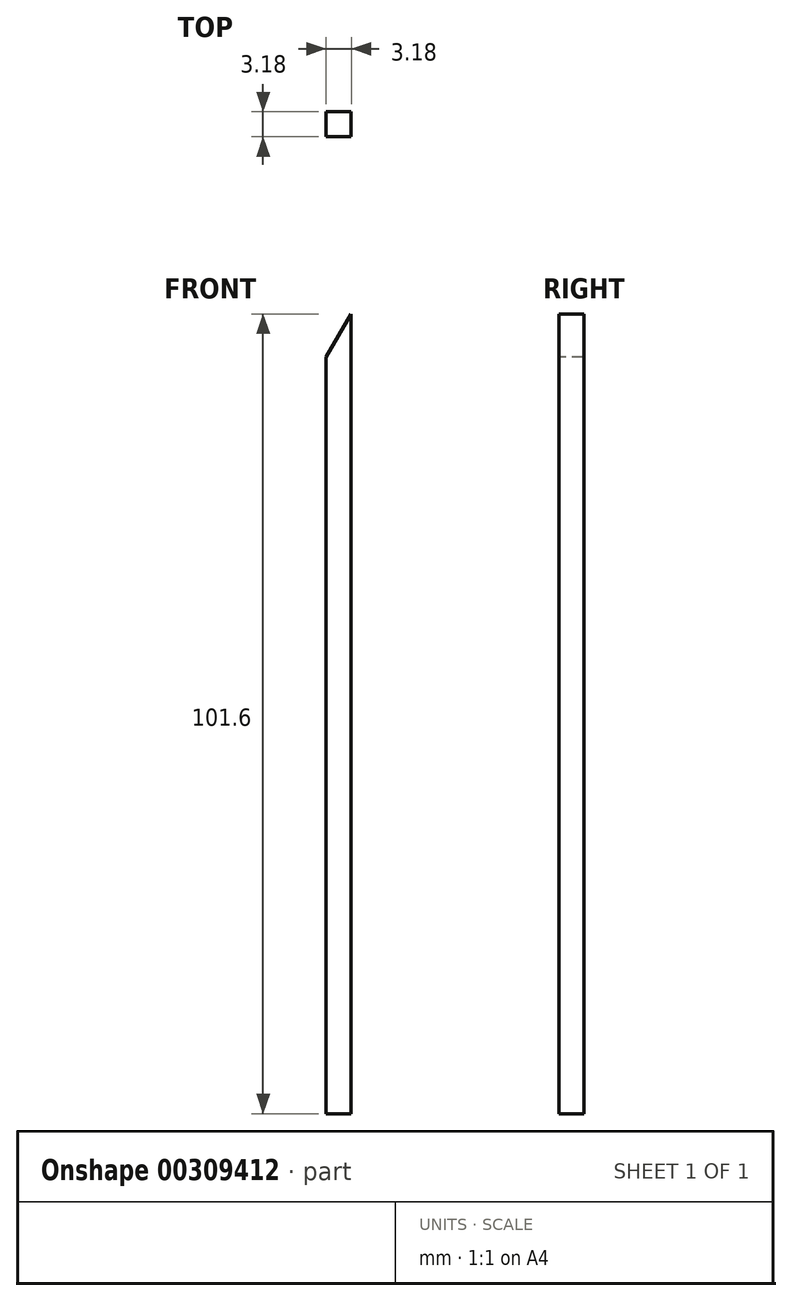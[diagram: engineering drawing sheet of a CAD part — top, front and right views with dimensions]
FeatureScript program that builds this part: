
annotation { "Feature Type Name" : "Feature", "Feature Type Description" : "" }
export const myFeature = defineFeature(function(context is Context, id is Id, definition is map)
    precondition{}
    {
        {
            var Q0;
            Q0=qCreatedBy(makeId("Front.planeOp"),FACE);
            var sketch = newSketch(context, id + "F0", { "sketchPlane" : qUnion([Q0])});
            skLineSegment(sketch, "E0.bottom", {"start": v(-1.59, 50.8) * mm, "end": v(1.59, 50.8) * mm});
            skLineSegment(sketch, "E0.top", {"start": v(-1.59, -50.8) * mm, "end": v(1.59, -50.8) * mm});
            skLineSegment(sketch, "E0.left", {"start": v(-1.59, 50.8) * mm, "end": v(-1.59, -50.8) * mm});
            skLineSegment(sketch, "E0.right", {"start": v(1.59, 50.8) * mm, "end": v(1.59, -50.8) * mm});
            skPoint(sketch, "E0.middle", {"position": v(0, 0) * mm});
            skSolve(sketch);
        }
        {
            var Q0;
            Q0 = qSketchRegion(id + "F0", true);
            extrude(context, id + "F1", {"entities" : qUnion([Q0]), "depth" : 3.17 * mm});
        }
        {
            var Q0;
            Q0=makeQuery(id+"F1.opExtrude","CAP_FACE",FACE,{"disambiguationData":[OSD([sQuery(id+"F0.wireOp",EDGE,"E0.bottom"),sQuery(id+"F0.wireOp",EDGE,"E0.top"),sQuery(id+"F0.wireOp",EDGE,"E0.left"),sQuery(id+"F0.wireOp",EDGE,"E0.right")])],"isStart":false});
            var sketch = newSketch(context, id + "F2", { "sketchPlane" : qUnion([Q0])});
            skLineSegment(sketch, "E1", {"start": v(1.59, 50.8) * mm, "end": v(-1.59, 45.3) * mm});
            skLineSegment(sketch, "E2", {"start": v(-1.59, 45.3) * mm, "end": v(-1.59, 50.8) * mm});
            skLineSegment(sketch, "E3", {"start": v(-1.59, 50.8) * mm, "end": v(1.59, 50.8) * mm});
            skSolve(sketch);
        }
        {
            var Q0;
            Q0 = qSketchRegion(id + "F2", true);
            extrude(context, id + "F3", {"entities" : qUnion([Q0]), "operationType" : NewBodyOperationType.REMOVE, "oppositeDirection" : true, "depth" : 25.4 * mm});
        }
    });
